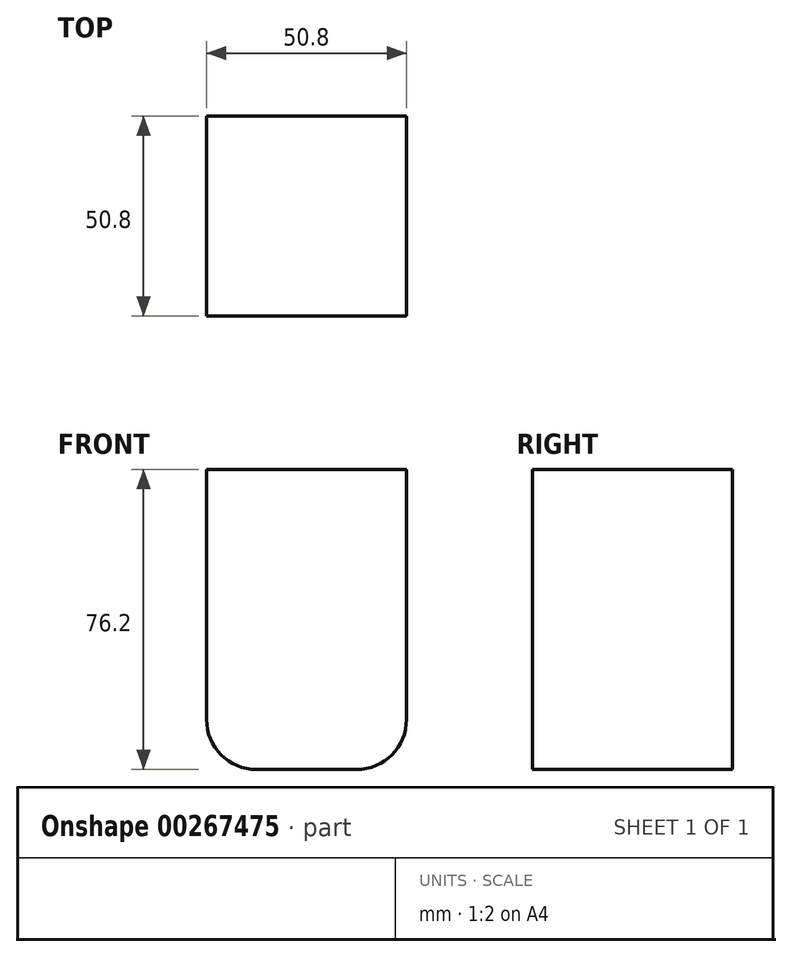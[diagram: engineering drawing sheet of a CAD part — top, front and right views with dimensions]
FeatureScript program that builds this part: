
annotation { "Feature Type Name" : "Feature", "Feature Type Description" : "" }
export const myFeature = defineFeature(function(context is Context, id is Id, definition is map)
    precondition{}
    {
        {
            var Q0;
            Q0=qCreatedBy(makeId("Front.planeOp"),FACE);
            var sketch = newSketch(context, id + "F0", { "sketchPlane" : qUnion([Q0])});
            skLineSegment(sketch, "E0.bottom", {"start": v(25.4, 38.1) * mm, "end": v(-25.4, 38.1) * mm});
            skLineSegment(sketch, "E0.top", {"start": v(25.4, -38.1) * mm, "end": v(-25.4, -38.1) * mm});
            skLineSegment(sketch, "E0.left", {"start": v(25.4, 38.1) * mm, "end": v(25.4, -38.1) * mm});
            skLineSegment(sketch, "E0.right", {"start": v(-25.4, 38.1) * mm, "end": v(-25.4, -38.1) * mm});
            skPoint(sketch, "E0.middle", {"position": v(0, 0) * mm});
            skSolve(sketch);
        }
        {
            var Q0;
            Q0 = qSketchRegion(id + "F0", true);
            extrude(context, id + "F1", {"entities" : qUnion([Q0]), "depth" : 50.8 * mm});
        }
        {
            var Q0;
            Q0=makeQuery(id+"F1.opExtrude","SWEPT_EDGE",EDGE,{"disambiguationData":[OSD([sQuery(id+"F0.wireOp",EDGE,"E0.top"),sQuery(id+"F0.wireOp",EDGE,"E0.right")])]});
            var Q1;
            Q1=makeQuery(id+"F1.opExtrude","SWEPT_EDGE",EDGE,{"disambiguationData":[OSD([sQuery(id+"F0.wireOp",EDGE,"E0.top"),sQuery(id+"F0.wireOp",EDGE,"E0.left")])]});
            fillet(context, id + "F2", {"entities" : qUnion([Q0, Q1]), "radius" : 12.7 * mm, "tangentPropagation" : true, "allowEdgeOverflow" : false});
        }
    });
